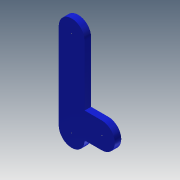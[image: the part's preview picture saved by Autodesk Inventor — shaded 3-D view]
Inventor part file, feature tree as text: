
AUTODESK INVENTOR PART (.ipt)
format: ipt  version: 2013 (Build 170138000, 138)  size: 131,584 bytes
history: native  units: mm
features: extrude x5, sketch x5
ambient origin geometry x8: Origin, YZ Plane, XZ Plane, XY Plane, X Axis, Y Axis, Z Axis, Center Point
bodies: Solid1 (feature_tree)
feature tree (10):
  extrude  "Extrusion1"  Depth=20.0mm
  extrude  "Extrusion2"  Depth=6.0mm
  extrude  "Extrusion3"  Depth=4.0mm
  extrude  "Extrusion4"  Depth=3.0mm
  extrude  "Extrusion5"  Depth=1.5mm TaperAngle=0.0deg
  sketch  "Sketch1"  dims[d0=6.0mm d1=20.0mm]
  sketch  "Sketch2"  dims[d2=6.0mm d4=6.0mm]
  sketch  "Sketch3"  dims[d5=4.0mm d6=4.0mm]
  sketch  "Sketch4"  dims[d7=2.0mm d10=3.0mm]
  sketch  "Sketch5"  dims[d11=6.0mm d12=1.5mm d13=0.0mm d14=3.0mm d15=3.0mm d16=4.0mm d17=6.0mm d18=1.5mm d19=0.0mm d20=4.0mm d21=6.0mm d22=4.0mm d23=1.5mm d24=0.0mm d25=3.0mm d26=1.5mm d27=0.0mm d28=0.2mm d29=0.2mm d30=0.2mm d31=1.5mm d32=0.0mm]
